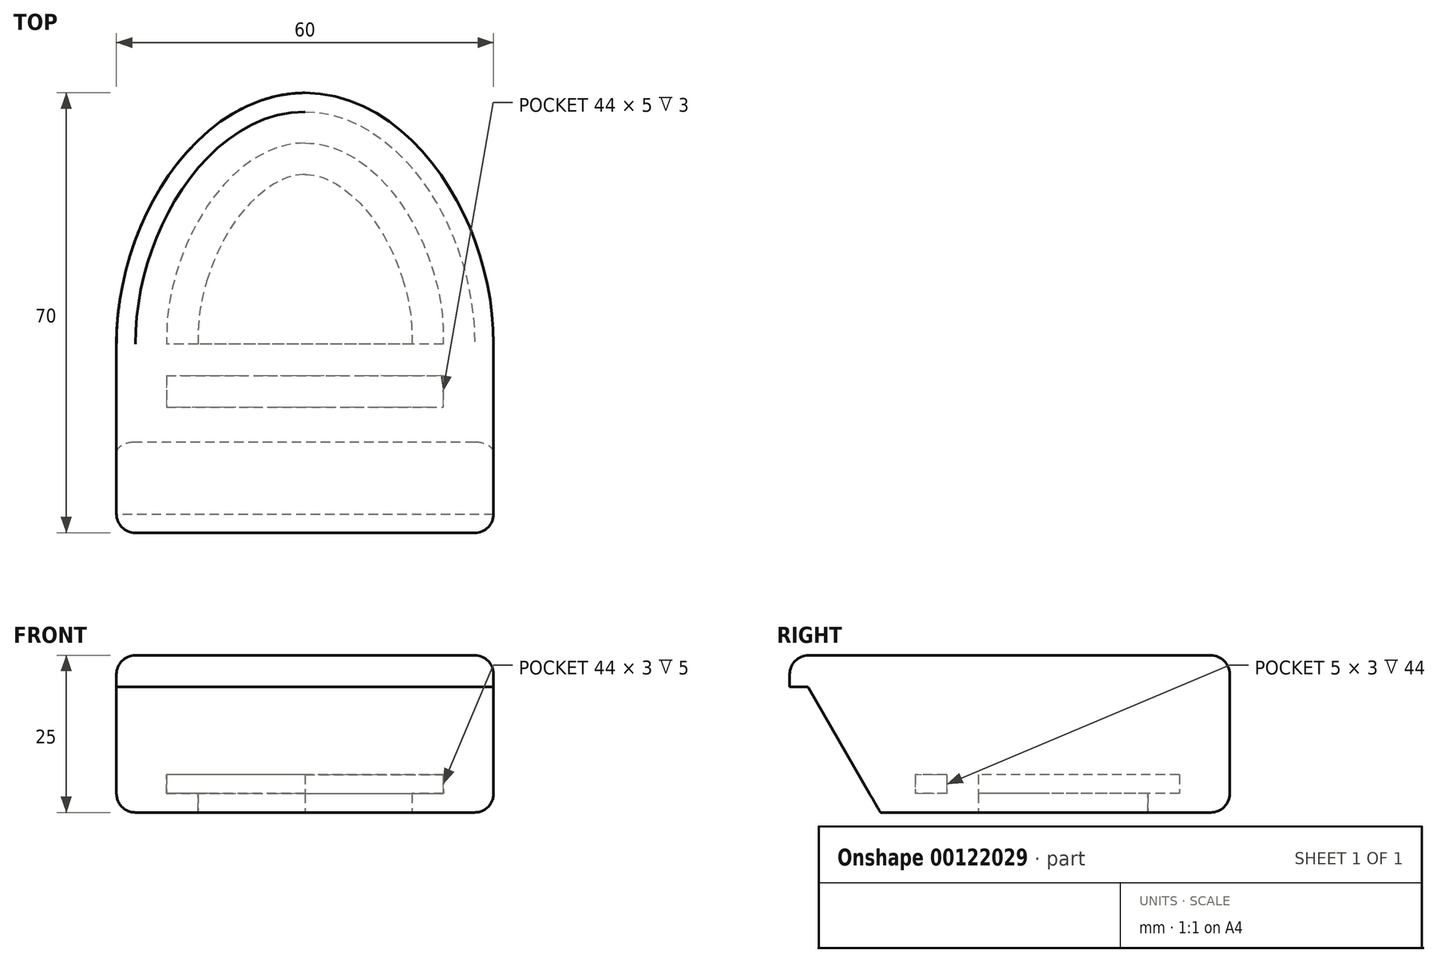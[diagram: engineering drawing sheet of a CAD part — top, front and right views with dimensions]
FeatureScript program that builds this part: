
annotation { "Feature Type Name" : "Feature", "Feature Type Description" : "" }
export const myFeature = defineFeature(function(context is Context, id is Id, definition is map)
    precondition{}
    {
        {
            var Q0;
            Q0=qCreatedBy(makeId("Top.planeOp"),FACE);
            var sketch = newSketch(context, id + "F0", { "sketchPlane" : qUnion([Q0])});
            skLineSegment(sketch, "E0.top", {"start": v(-30, -30) * mm, "end": v(30, -30) * mm});
            skPoint(sketch, "E0.middle", {"position": v(0, 0) * mm});
            skPoint(sketch, "E1.visualSharp", {"position": v(-30, -30) * mm});
            skPoint(sketch, "E2.visualSharp", {"position": v(30, -30) * mm});
            skPoint(sketch, "E3", {"position": v(-30, 0) * mm});
            skPoint(sketch, "E4", {"position": v(30, 10) * mm});
            skFitSpline(sketch, "E5", {"points": [v(0, 40) * mm, v(-30, 0) * mm], "startDerivative": vector(-49.89, 0) * mm, "endDerivative": vector(0, -60.15) * mm});
            skLineSegment(sketch, "E6", {"start": v(-30, 0) * mm, "end": v(-30, -30) * mm});
            skLineSegment(sketch, "E7", {"start": v(30, 10) * mm, "end": v(30, -30) * mm});
            skFitSpline(sketch, "E8.MirrorCS", {"points": [v(0, 40) * mm, v(30, 0) * mm], "startDerivative": vector(49.89, 0) * mm, "endDerivative": vector(0, -60.15) * mm});
            skSolve(sketch);
        }
        {
            var Q0;
            Q0=qSketchRegion(id+"F0",true);
            extrude(context, id + "F1", {"entities" : qUnion([Q0]), "endBound" : BoundingType.SYMMETRIC, "depth" : 25 * mm});
        }
        {
            var Q0;
            Q0=makeQuery(id+"F1.opExtrude","CAP_EDGE",EDGE,{"disambiguationData":[OSD([sQuery(id+"F0.wireOp",EDGE,"E7")])],"isStart":true});
            var Q1;
            Q1=makeQuery(id+"F1.opExtrude","CAP_EDGE",EDGE,{"disambiguationData":[OSD([sQuery(id+"F0.wireOp",EDGE,"E7")])],"isStart":false});
            var Q2;
            Q2=makeQuery(id+"F1.opExtrude","CAP_EDGE",EDGE,{"disambiguationData":[OSD([sQuery(id+"F0.wireOp",EDGE,"E6")])],"isStart":false});
            var Q3;
            Q3=makeQuery(id+"F1.opExtrude","CAP_EDGE",EDGE,{"disambiguationData":[OSD([sQuery(id+"F0.wireOp",EDGE,"E6")])],"isStart":true});
            fillet(context, id + "F2", {"entities" : qUnion([Q0, Q1, Q2, Q3]), "radius" : 3 * mm, "tangentPropagation" : true, "allowEdgeOverflow" : false});
        }
        {
            var Q0;
            Q0=qCreatedBy(makeId("Right.planeOp"),FACE);
            var sketch = newSketch(context, id + "F3", { "sketchPlane" : qUnion([Q0])});
            skLineSegment(sketch, "E9", {"start": v(0, 0) * mm, "end": v(-30, 0) * mm});
            skPoint(sketch, "E10", {"position": v(-30, 0) * mm});
            skLineSegment(sketch, "E11", {"start": v(-30, 12.5) * mm, "end": v(-30, -12.5) * mm});
            skLineSegment(sketch, "E12", {"start": v(-30, -12.5) * mm, "end": v(0, -12.5) * mm});
            skLineSegment(sketch, "E13", {"start": v(-30, 12.5) * mm, "end": v(-15.57, -12.5) * mm});
            skLineSegment(sketch, "E14", {"start": v(-30, 7.5) * mm, "end": v(-27.11, 7.5) * mm});
            skSolve(sketch);
        }
        {
            var Q0;
            {var subQ0=sQuery(id+"F3.wireOp",EDGE,"E11");var subQ1=sQuery(id+"F3.wireOp",EDGE,"E9");var subQ2=makeQuery(id+"F3.imprint","INTERSECT",VERTEX,{"derivedFrom":[subQ1,subQ0]});Q0=makeQuery(id+"F3.imprint","IMPRINT",FACE,{"disambiguationData":[TD([[makeQuery(id+"F3.imprint","IMPRINT",EDGE,{"disambiguationData":[TD([[subQ2,1.0]])],"derivedFrom":subQ1}),1.0]])]});}
            var Q1;
            {var subQ0=sQuery(id+"F3.wireOp",EDGE,"E11");var subQ1=sQuery(id+"F3.wireOp",EDGE,"E9");var subQ2=makeQuery(id+"F3.imprint","INTERSECT",VERTEX,{"derivedFrom":[subQ1,subQ0]});Q1=makeQuery(id+"F3.imprint","IMPRINT",FACE,{"disambiguationData":[TD([[makeQuery(id+"F3.imprint","IMPRINT",EDGE,{"disambiguationData":[TD([[subQ2,1.0]])],"derivedFrom":subQ1}),-1.0]])]});}
            extrude(context, id + "F4", {"entities" : qUnion([Q0, Q1]), "operationType" : NewBodyOperationType.REMOVE, "endBound" : BoundingType.SYMMETRIC, "depth" : 60 * mm});
        }
        {
            var Q0;
            Q0=makeQuery(id+"F1.opExtrude","CAP_FACE",FACE,{"disambiguationData":[OSD([sQuery(id+"F0.wireOp",EDGE,"E0.top"),sQuery(id+"F0.wireOp",EDGE,"E5"),sQuery(id+"F0.wireOp",EDGE,"5cda4a63-8e27-4d9c-be18-28a9360ed2950.MirrorCS"),sQuery(id+"F0.wireOp",EDGE,"E6"),sQuery(id+"F0.wireOp",EDGE,"E7")])],"isStart":true});
            var sketch = newSketch(context, id + "F5", { "sketchPlane" : qUnion([Q0])});
            skLineSegment(sketch, "E15.bottom", {"start": v(30, 0) * mm, "end": v(-30, 0) * mm});
            skLineSegment(sketch, "E15.top", {"start": v(30, 15.57) * mm, "end": v(-30, 15.57) * mm});
            skLineSegment(sketch, "E15.left", {"start": v(30, 0) * mm, "end": v(30, 15.57) * mm});
            skLineSegment(sketch, "E15.right", {"start": v(-30, 0) * mm, "end": v(-30, 15.57) * mm});
            skFitSpline(sketch, "E16", {"points": [v(0, -40) * mm, v(30, 0) * mm], "startDerivative": vector(49.89, 0) * mm, "endDerivative": vector(0, 60.15) * mm});
            skFitSpline(sketch, "E17.MirrorCS", {"points": [v(0, -40) * mm, v(-30, 0) * mm], "startDerivative": vector(-49.89, 0) * mm, "endDerivative": vector(0, 60.15) * mm});
            skFitSpline(sketch, "E18.0", {"points": [v(0, -32) * mm, v(0.64, -32) * mm, v(1.9, -31.9) * mm, v(3.77, -31.49) * mm, v(5.66, -30.78) * mm, v(8.18, -29.45) * mm, v(11.32, -27.03) * mm, v(14.84, -22.99) * mm, v(17.86, -18) * mm, v(20.18, -12.32) * mm, v(21.66, -6.22) * mm, v(22, -2.06) * mm, v(22, 0) * mm]});
            skFitSpline(sketch, "E18.1", {"points": [v(0, -32) * mm, v(-0.64, -32) * mm, v(-1.9, -31.9) * mm, v(-3.77, -31.49) * mm, v(-5.66, -30.78) * mm, v(-8.18, -29.45) * mm, v(-11.32, -27.03) * mm, v(-14.84, -22.99) * mm, v(-17.86, -18) * mm, v(-20.18, -12.32) * mm, v(-21.66, -6.22) * mm, v(-22, -2.06) * mm, v(-22, 0) * mm]});
            skFitSpline(sketch, "E19.0", {"points": [v(0, -27) * mm, v(0.4, -27) * mm, v(1.15, -26.94) * mm, v(2.33, -26.68) * mm, v(3.59, -26.21) * mm, v(4.94, -25.5) * mm, v(6.36, -24.53) * mm, v(8.32, -22.85) * mm, v(10.76, -20.06) * mm, v(13.36, -15.76) * mm, v(15.4, -10.78) * mm, v(16.7, -5.42) * mm, v(17, -1.78) * mm, v(17, 0) * mm]});
            skFitSpline(sketch, "E19.1", {"points": [v(0, -27) * mm, v(-0.4, -27) * mm, v(-1.15, -26.94) * mm, v(-2.33, -26.68) * mm, v(-3.59, -26.21) * mm, v(-4.94, -25.5) * mm, v(-6.36, -24.53) * mm, v(-8.32, -22.85) * mm, v(-10.76, -20.06) * mm, v(-13.36, -15.76) * mm, v(-15.4, -10.78) * mm, v(-16.7, -5.42) * mm, v(-17, -1.78) * mm, v(-17, 0) * mm]});
            skLineSegment(sketch, "E20.bottom", {"start": v(-22, 0) * mm, "end": v(22, 0) * mm});
            skLineSegment(sketch, "E20.top", {"start": v(-22, 10) * mm, "end": v(22, 10) * mm});
            skLineSegment(sketch, "E20.left", {"start": v(-22, 0) * mm, "end": v(-22, 10) * mm});
            skLineSegment(sketch, "E20.right", {"start": v(22, 0) * mm, "end": v(22, 10) * mm});
            skLineSegment(sketch, "E21", {"start": v(-20.56, -10.51) * mm, "end": v(-15.34, -10.51) * mm});
            skLineSegment(sketch, "E22.MirrorCS", {"start": v(20.56, -10.51) * mm, "end": v(15.34, -10.51) * mm});
            skLineSegment(sketch, "E23.top", {"start": v(-22, 5) * mm, "end": v(22, 5) * mm});
            skLineSegment(sketch, "E23.left", {"start": v(-22, 10) * mm, "end": v(-22, 5) * mm});
            skLineSegment(sketch, "E23.right", {"start": v(22, 10) * mm, "end": v(22, 5) * mm});
            skSolve(sketch);
        }
        {
            var Q0;
            Q0=makeQuery(id+"F5.imprint","IMPRINT",FACE,{"disambiguationData":[TD([[makeQuery(id+"F5.imprint","IMPRINT",EDGE,{"derivedFrom":sQuery(id+"F5.wireOp",EDGE,"E20.top")}),-1.0]])]});
            var Q1;
            {var subQ0=sQuery(id+"F5.wireOp",EDGE,"E20.left");Q1=makeQuery(id+"F5.imprint","IMPRINT",FACE,{"disambiguationData":[TD([[makeQuery(id+"F5.imprint","IMPRINT",EDGE,{"derivedFrom":subQ0}),-1.0]])]});}
            var Q2;
            {var subQ1=sQuery(id+"F5.wireOp",EDGE,"E19.1");var subQ4=sQuery(id+"F5.wireOp",EDGE,"E19.0");var subQ5=makeQuery(id+"F5.imprint","INTERSECT",VERTEX,{"derivedFrom":[subQ4,subQ1]});Q2=makeQuery(id+"F5.imprint","IMPRINT",FACE,{"disambiguationData":[TD([[makeQuery(id+"F5.imprint","IMPRINT",EDGE,{"disambiguationData":[TD([[subQ5,-1.0]])],"derivedFrom":subQ4}),1.0]])]});}
            var Q3;
            {var subQ0=sQuery(id+"F5.wireOp",EDGE,"E20.bottom");var subQ5=sQuery(id+"F5.wireOp",EDGE,"E19.1");var subQ6=makeQuery(id+"F5.imprint","INTERSECT",VERTEX,{"derivedFrom":[subQ5,subQ0]});Q3=makeQuery(id+"F5.imprint","IMPRINT",FACE,{"disambiguationData":[TD([[makeQuery(id+"F5.imprint","IMPRINT",EDGE,{"disambiguationData":[TD([[subQ6,1.0]])],"derivedFrom":subQ5}),1.0]])]});}
            var Q4;
            {var subQ5=sQuery(id+"F5.wireOp",EDGE,"E18.1");var subQ9=sQuery(id+"F5.wireOp",EDGE,"E18.0");var subQ10=makeQuery(id+"F5.imprint","INTERSECT",VERTEX,{"derivedFrom":[subQ9,subQ5]});Q4=makeQuery(id+"F5.imprint","IMPRINT",FACE,{"disambiguationData":[TD([[makeQuery(id+"F5.imprint","IMPRINT",EDGE,{"disambiguationData":[TD([[subQ10,-1.0]])],"derivedFrom":subQ9}),1.0]])]});}
            var Q5;
            {var subQ0=sQuery(id+"F5.wireOp",EDGE,"E20.bottom");var subQ5=sQuery(id+"F5.wireOp",EDGE,"E19.0");var subQ6=makeQuery(id+"F5.imprint","INTERSECT",VERTEX,{"derivedFrom":[subQ5,subQ0]});Q5=makeQuery(id+"F5.imprint","IMPRINT",FACE,{"disambiguationData":[TD([[makeQuery(id+"F5.imprint","IMPRINT",EDGE,{"disambiguationData":[TD([[subQ6,1.0]])],"derivedFrom":subQ5}),-1.0]])]});}
            extrude(context, id + "F6", {"entities" : qUnion([Q0, Q1, Q2, Q3, Q4, Q5]), "operationType" : NewBodyOperationType.REMOVE, "oppositeDirection" : true, "depth" : 6 * mm});
        }
        {
            var Q0;
            {var subQ5=sQuery(id+"F5.wireOp",EDGE,"E18.1");var subQ9=sQuery(id+"F5.wireOp",EDGE,"E18.0");var subQ10=makeQuery(id+"F5.imprint","INTERSECT",VERTEX,{"derivedFrom":[subQ9,subQ5]});Q0=makeQuery(id+"F5.imprint","IMPRINT",FACE,{"disambiguationData":[TD([[makeQuery(id+"F5.imprint","IMPRINT",EDGE,{"disambiguationData":[TD([[subQ10,-1.0]])],"derivedFrom":subQ9}),1.0]])]});}
            var Q1;
            Q1=makeQuery(id+"F5.imprint","IMPRINT",FACE,{"disambiguationData":[TD([[makeQuery(id+"F5.imprint","IMPRINT",EDGE,{"derivedFrom":sQuery(id+"F5.wireOp",EDGE,"E20.top")}),-1.0]])]});
            extrude(context, id + "F7", {"entities" : qUnion([Q0, Q1]), "operationType" : NewBodyOperationType.ADD, "oppositeDirection" : true, "depth" : 3 * mm});
        }
        {
            var Q0;
            Q0=makeQuery(id+"F1.opExtrude","CAP_EDGE",EDGE,{"disambiguationData":[OSD([sQuery(id+"F0.wireOp",EDGE,"E0.top")])],"isStart":false});
            fillet(context, id + "F8", {"entities" : qUnion([Q0]), "radius" : 3 * mm, "tangentPropagation" : true, "allowEdgeOverflow" : false});
        }
    });
